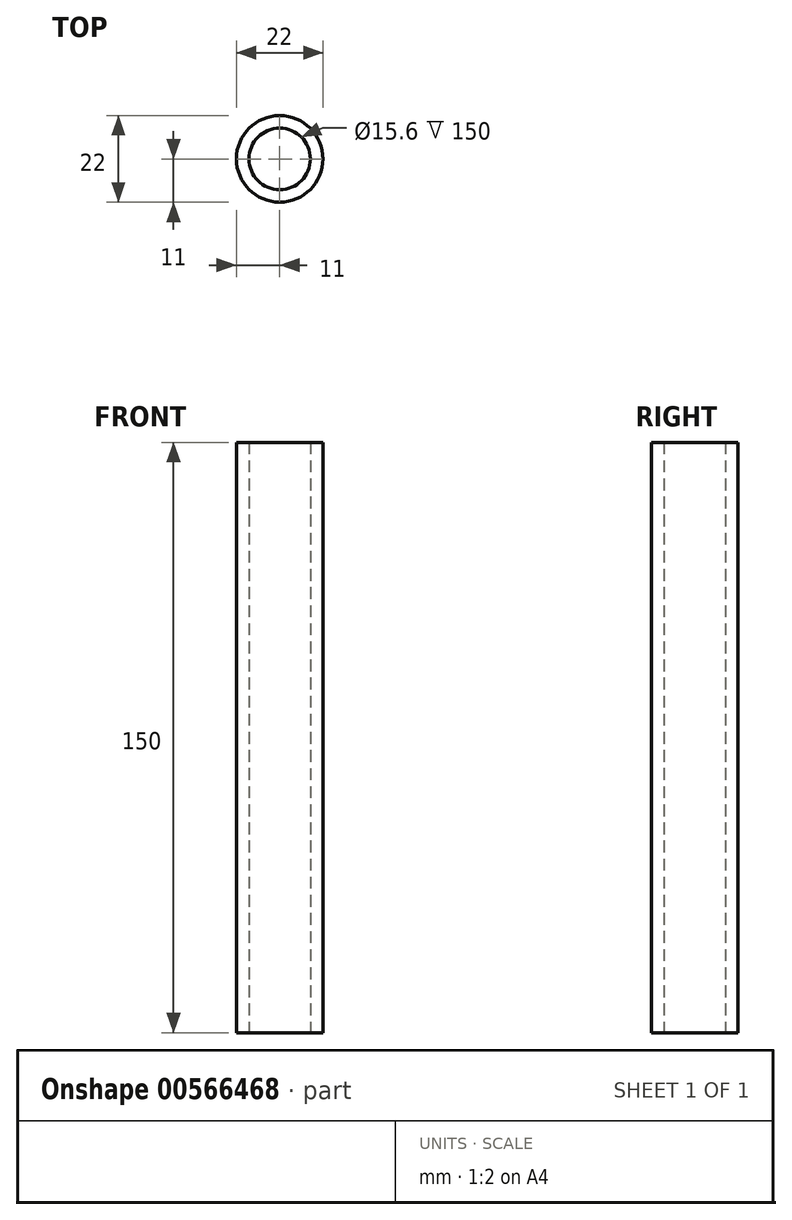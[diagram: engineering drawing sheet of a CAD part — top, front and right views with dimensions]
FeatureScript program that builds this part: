
annotation { "Feature Type Name" : "Feature", "Feature Type Description" : "" }
export const myFeature = defineFeature(function(context is Context, id is Id, definition is map)
    precondition{}
    {
        {
            var Q0;
            Q0=qCreatedBy(makeId("Top.planeOp"),FACE);
            var sketch = newSketch(context, id + "F0", { "sketchPlane" : qUnion([Q0])});
            skCircle(sketch, "E0", {"center": v(0, 0) * mm, "radius": 7.8 * mm});
            skCircle(sketch, "E1", {"center": v(0, 0) * mm, "radius": 11 * mm});
            skSolve(sketch);
        }
        {
            var Q0;
            Q0=qSketchRegion(id+"F0",true);
            extrude(context, id + "F1", {"entities" : qUnion([Q0]), "depth" : 150 * mm});
        }
    });
